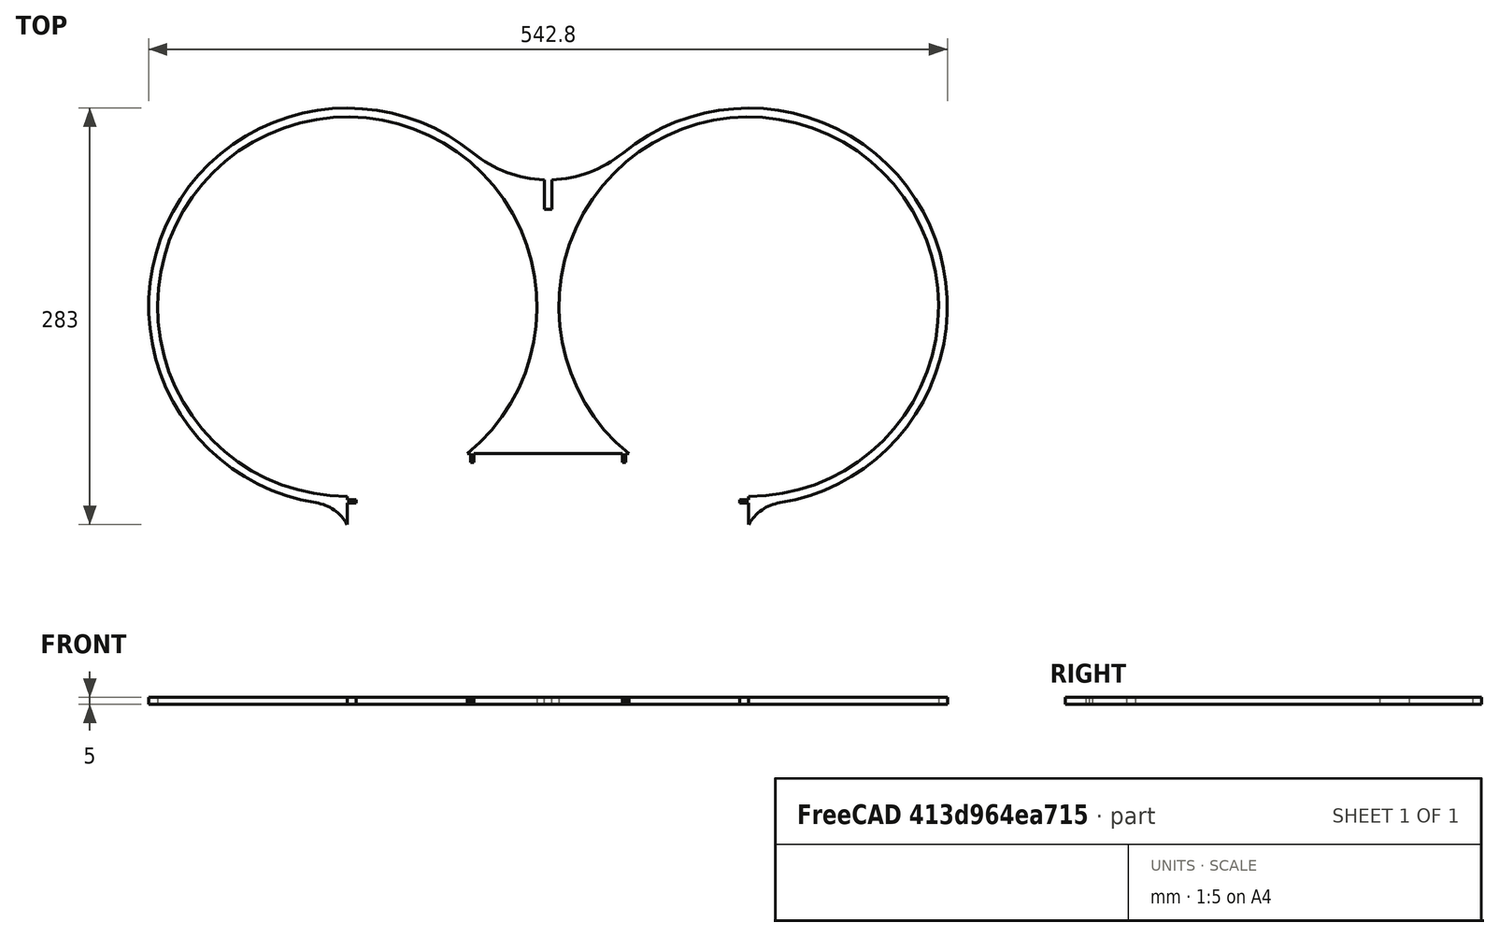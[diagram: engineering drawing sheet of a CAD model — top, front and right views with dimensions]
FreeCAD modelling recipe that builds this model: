
FCSTD DOCUMENT  (FreeCAD 0.16R6706 (Git))
Label: cut_fan
License: All rights reserved
LicenseURL: http://en.wikipedia.org/wiki/All_rights_reserved
objects: Sketcher::SketchObject×3, PartDesign::Pad×1, Part::Part2DObjectPython×1
note: 6 computed .brp shape members not serialized (recipe doc carries the construction recipe); baked Part::Feature solids carry a one-line shape summary decoded from their .brp

FEATURE [Sketcher::SketchObject] Sketch
  sketch-geometry (35):
    g0: ArcOfCircle CenterX=136.4 CenterY=150 CenterZ=0 NormalX=0 NormalY=0 NormalZ=1 Radius=129 StartAngle=4.71231 EndAngle=10.3118
    g1: ArcOfCircle CenterX=-136.4 CenterY=150 CenterZ=0 NormalX=0 NormalY=0 NormalZ=1 Radius=129 StartAngle=5.39616 EndAngle=10.9957
    g2: LineSegment [constr] StartX=-136.39 StartY=2.00014 StartZ=0 EndX=136.39 EndY=2.00014 EndZ=0
    g3: ArcOfCircle CenterX=0 CenterY=316.193 CenterZ=0 NormalX=0 NormalY=0 NormalZ=1 Radius=80 StartAngle=4.02513 EndAngle=4.68113
    g4: ArcOfCircle CenterX=162.407 CenterY=-12.9376 CenterZ=0 NormalX=0 NormalY=0 NormalZ=1 Radius=30 StartAngle=1.72907 EndAngle=2.62039
    g5: ArcOfCircle CenterX=-162.407 CenterY=-12.9376 CenterZ=0 NormalX=0 NormalY=0 NormalZ=1 Radius=30 StartAngle=0.521204 EndAngle=1.41252
    g6: ArcOfCircle CenterX=-136.4 CenterY=150 CenterZ=0 NormalX=0 NormalY=0 NormalZ=1 Radius=135 StartAngle=0.88354 EndAngle=4.55411
    g7: ArcOfCircle CenterX=136.4 CenterY=150 CenterZ=0 NormalX=0 NormalY=0 NormalZ=1 Radius=135 StartAngle=4.87066 EndAngle=8.54124
    g8: LineSegment [constr] StartX=-136.39 StartY=2.00014 StartZ=0 EndX=-136.39 EndY=50 EndZ=0
    g9: LineSegment StartX=-136.39 StartY=21 StartZ=0 EndX=-136.39 EndY=18.7 EndZ=0
    g10: LineSegment StartX=-136.39 StartY=18.7 StartZ=0 EndX=-130.39 EndY=18.7 EndZ=0
    g11: LineSegment StartX=-130.39 StartY=18.7 StartZ=0 EndX=-130.39 EndY=16.5 EndZ=0
    g12: LineSegment StartX=-130.39 StartY=16.5 StartZ=0 EndX=-136.39 EndY=16.5 EndZ=0
    g13: LineSegment [constr] StartX=136.39 StartY=50 StartZ=0 EndX=-136.39 EndY=50 EndZ=0
    g14: LineSegment StartX=-54.9077 StartY=50 StartZ=0 EndX=-52.7077 EndY=50 EndZ=0
    g15: LineSegment StartX=-52.7077 StartY=50 StartZ=0 EndX=-52.7077 EndY=44 EndZ=0
    g16: LineSegment StartX=-52.7077 StartY=44 StartZ=0 EndX=-50.5077 EndY=44 EndZ=0
    g17: LineSegment StartX=-50.5077 StartY=44 StartZ=0 EndX=-50.5077 EndY=50 EndZ=0
    g18: LineSegment StartX=-50.5077 StartY=50 StartZ=0 EndX=50.5077 EndY=50 EndZ=0
    g19: LineSegment StartX=50.5077 StartY=50 StartZ=0 EndX=50.5077 EndY=44 EndZ=0
    g20: LineSegment StartX=50.5077 StartY=44 StartZ=0 EndX=52.7077 EndY=44 EndZ=0
    g21: LineSegment StartX=52.7077 StartY=44 StartZ=0 EndX=52.7077 EndY=50 EndZ=0
    g22: LineSegment StartX=52.7077 StartY=50 StartZ=0 EndX=54.9077 EndY=50 EndZ=0
    g23: LineSegment [constr] StartX=136.39 StartY=50 StartZ=0 EndX=136.39 EndY=2.00014 EndZ=0
    g24: LineSegment StartX=136.39 StartY=21 StartZ=0 EndX=136.39 EndY=18.7 EndZ=0
    g25: LineSegment StartX=136.39 StartY=18.7 StartZ=0 EndX=130.39 EndY=18.7 EndZ=0
    g26: LineSegment StartX=130.39 StartY=18.7 StartZ=0 EndX=130.39 EndY=16.5 EndZ=0
    g27: LineSegment StartX=130.39 StartY=16.5 StartZ=0 EndX=136.39 EndY=16.5 EndZ=0
    g28: LineSegment StartX=136.39 StartY=16.5 StartZ=0 EndX=136.39 EndY=2.00014 EndZ=0
    g29: LineSegment [constr] StartX=-2.5 StartY=236.232 StartZ=0 EndX=2.5 EndY=236.232 EndZ=0
    g30: LineSegment StartX=2.5 StartY=236.232 StartZ=0 EndX=2.5 EndY=216.232 EndZ=0
    g31: LineSegment StartX=2.5 StartY=216.232 StartZ=0 EndX=-2.5 EndY=216.232 EndZ=0
    g32: LineSegment StartX=-2.5 StartY=216.232 StartZ=0 EndX=-2.5 EndY=236.232 EndZ=0
    g33: ArcOfCircle CenterX=0 CenterY=316.193 CenterZ=0 NormalX=0 NormalY=0 NormalZ=1 Radius=80 StartAngle=4.74364 EndAngle=5.39965
    g34: LineSegment StartX=-136.39 StartY=16.5 StartZ=0 EndX=-136.39 EndY=2.00014 EndZ=0
  constraints (105):
    c: Equal(g1,g0)
    c: Symmetric(g0,g1,g-2)
    c: Radius(g0) = 129
    c: DistanceX(g0) = 136.4
    c: DistanceY(g0) = 150
    c: Horizontal(g2)
    c: Symmetric(g2,g2,g-2)
    c: PointOnObject(g3,g-2)
    c: Radius(g3) = 80
    c: Coincident(g4,g2)
    c: Equal(g5,g4)
    c: Radius(g5) = 30
    c: DistanceY(g-1,g13) = 50
    c: Coincident(g6,g1)
    c: Coincident(g6,g5)
    c: Coincident(g6,g3)
    c: Coincident(g7,g0)
    c: Coincident(g7,g4)
    c: Coincident(g7,g33)
    c: Radius(g6) = 135
    c: Radius(g7) = 135
    c: Tangent(g3,g6)
    c: Tangent(g33,g7) = 1.5708
    c: Tangent(g4,g7) = 1.5708
    c: Tangent(g5,g6) = 1.5708
    c: Coincident(g8,g2)
    c: Vertical(g8)
    c: PointOnObject(g1,g8)
    c: Coincident(g9,g1)
    c: PointOnObject(g9,g8)
    c: Coincident(g10,g9)
    c: Horizontal(g10)
    c: Coincident(g11,g10)
    c: Vertical(g11)
    c: PointOnObject(g12,g8)
    c: Horizontal(g12)
    c: Coincident(g11,g12)
    c: Coincident(g13,g8)
    c: Horizontal(g13)
    c: PointOnObject(g1,g13)
    c: PointOnObject(g0,g13)
    c: Coincident(g14,g1)
    c: PointOnObject(g14,g13)
    c: Coincident(g15,g14)
    c: Vertical(g15)
    c: Coincident(g16,g15)
    c: Coincident(g17,g16)
    c: PointOnObject(g17,g13)
    c: Coincident(g18,g17)
    c: PointOnObject(g18,g13)
    c: Coincident(g19,g18)
    c: Vertical(g19)
    c: Coincident(g20,g19)
    c: PointOnObject(g21,g13)
    c: Coincident(g22,g21)
    c: Coincident(g22,g0)
    c: Vertical(g21)
    c: Vertical(g17)
    c: Horizontal(g20)
    c: Horizontal(g16)
    c: Coincident(g20,g21)
    c: Coincident(g23,g13)
    c: Coincident(g23,g2)
    c: Vertical(g23)
    c: PointOnObject(g0,g23)
    c: Coincident(g24,g0)
    c: PointOnObject(g24,g23)
    c: Coincident(g25,g24)
    c: Horizontal(g25)
    c: Coincident(g26,g25)
    c: Vertical(g26)
    c: Coincident(g27,g26)
    c: PointOnObject(g27,g23)
    c: Horizontal(g27)
    c: Coincident(g28,g27)
    c: Coincident(g28,g2)
    c: Equal(g25,g19)
    c: Equal(g19,g17)
    c: Equal(g17,g10)
    c: Equal(g11,g16)
    c: Equal(g16,g20)
    c: Equal(g20,g26)
    c: Symmetric(g19,g16,g-2)
    c: Symmetric(g25,g10,g-2)
    c: Distance(g26) = 2.2
    c: DistanceY(g9,g1) = 2.3
    c: Distance(g12) = 6
    c: DistanceX(g1,g15) = 2.2
    c: Coincident(g30,g31)
    c: Coincident(g31,g32)
    c: Horizontal(g29)
    c: Horizontal(g31)
    c: Vertical(g30)
    c: Vertical(g32)
    c: PointOnObject(g32,g3)
    c: Distance(g31) = 5
    c: Distance(g30) = 20
    c: PointOnObject(g30,g3)
    c: Equal(g3,g33)
    c: Coincident(g3,g29)
    c: Coincident(g33,g29)
    c: Coincident(g3,g33)
    c: Coincident(g2,g5)
    c: Coincident(g34,g12)
    c: Coincident(g34,g2)
FEATURE [PartDesign::Pad] Pad
  Length = 5
  Length2 = 100
  Sketch = -> Sketch
  Type = 0
FEATURE [Part::Part2DObjectPython] Shape2DView  # Draft 2D object (typed FeaturePython)
  Base = -> Pad
  FaceNumbers = [11]
  HiddenLines = false
  Projection = (0,0,1)
  ProjectionMode = 0
  SegmentLength = 0.05
  Tessellation = false
FEATURE [Sketcher::SketchObject] Sketch002
  sketch-geometry (28):
    g0: LineSegment StartX=-392.221 StartY=-72.7258 StartZ=0 EndX=-378.521 EndY=-72.7258 EndZ=0
    g1: LineSegment StartX=-122.221 StartY=-72.7258 StartZ=0 EndX=-122.221 EndY=-329.726 EndZ=0
    g2: LineSegment StartX=-122.221 StartY=-329.726 StartZ=0 EndX=-348.521 EndY=-329.726 EndZ=0
    g3: LineSegment StartX=-392.221 StartY=-329.726 StartZ=0 EndX=-392.221 EndY=-72.7258 EndZ=0
    g4: LineSegment StartX=-348.521 StartY=-72.7258 StartZ=0 EndX=-348.521 EndY=-87.7258 EndZ=0
    g5: LineSegment StartX=-369.521 StartY=-102.726 StartZ=0 EndX=-378.521 EndY=-102.726 EndZ=0
    g6: LineSegment StartX=-378.521 StartY=-102.726 StartZ=0 EndX=-378.521 EndY=-72.7258 EndZ=0
    g7: LineSegment StartX=-348.521 StartY=-329.726 StartZ=0 EndX=-348.521 EndY=-314.726 EndZ=0
    g8: LineSegment StartX=-369.521 StartY=-299.726 StartZ=0 EndX=-378.521 EndY=-299.726 EndZ=0
    g9: LineSegment StartX=-378.521 StartY=-299.726 StartZ=0 EndX=-378.521 EndY=-329.726 EndZ=0
    g10: LineSegment StartX=-132.221 StartY=-198.726 StartZ=0 EndX=-141.221 EndY=-198.726 EndZ=0
    g11: LineSegment StartX=-141.221 StartY=-198.726 StartZ=0 EndX=-141.221 EndY=-203.726 EndZ=0
    g12: LineSegment StartX=-141.221 StartY=-203.726 StartZ=0 EndX=-132.221 EndY=-203.726 EndZ=0
    g13: LineSegment StartX=-132.221 StartY=-203.726 StartZ=0 EndX=-132.221 EndY=-198.726 EndZ=0
    g14: LineSegment StartX=-191.221 StartY=-157.726 StartZ=0 EndX=-311.221 EndY=-157.726 EndZ=0
    g15: LineSegment StartX=-311.221 StartY=-157.726 StartZ=0 EndX=-311.221 EndY=-244.726 EndZ=0
    g16: LineSegment StartX=-311.221 StartY=-244.726 StartZ=0 EndX=-191.221 EndY=-244.726 EndZ=0
    g17: LineSegment StartX=-191.221 StartY=-244.726 StartZ=0 EndX=-191.221 EndY=-157.726 EndZ=0
    g18: LineSegment StartX=-378.521 StartY=-329.726 StartZ=0 EndX=-392.221 EndY=-329.726 EndZ=0
    g19: LineSegment StartX=-348.521 StartY=-72.7258 StartZ=0 EndX=-122.221 EndY=-72.7258 EndZ=0
    g20: LineSegment StartX=-369.521 StartY=-102.726 StartZ=0 EndX=-369.521 EndY=-87.7258 EndZ=0
    g21: LineSegment StartX=-369.521 StartY=-87.7258 StartZ=0 EndX=-348.521 EndY=-87.7258 EndZ=0
    g22: LineSegment StartX=-369.521 StartY=-299.726 StartZ=0 EndX=-369.521 EndY=-314.726 EndZ=0
    g23: LineSegment StartX=-369.521 StartY=-314.726 StartZ=0 EndX=-348.521 EndY=-314.726 EndZ=0
    g24: LineSegment [constr] StartX=-122.221 StartY=-201.226 StartZ=0 EndX=-392.221 EndY=-201.226 EndZ=0
    g25: LineSegment [constr] StartX=-257.221 StartY=-72.7258 StartZ=0 EndX=-257.221 EndY=-329.726 EndZ=0
    g26: GeomPoint [constr] X=-257.221 Y=-201.226 Z=0
    g27: GeomPoint [constr] X=-257.221 Y=-201.226 Z=0
  constraints (83):
    c: Coincident(g19,g1)
    c: Coincident(g1,g2)
    c: Coincident(g18,g3)
    c: Coincident(g3,g0)
    c: Horizontal(g0)
    c: Horizontal(g2)
    c: Vertical(g1)
    c: Vertical(g3)
    c: Coincident(g5,g6)
    c: Horizontal(g5)
    c: Vertical(g4)
    c: Vertical(g6)
    c: PointOnObject(g6,g0)
    c: Coincident(g8,g9)
    c: Horizontal(g8)
    c: Vertical(g7)
    c: Vertical(g9)
    c: PointOnObject(g9,g2)
    c: Coincident(g10,g11)
    c: Coincident(g11,g12)
    c: Coincident(g12,g13)
    c: Coincident(g13,g10)
    c: Horizontal(g10)
    c: Horizontal(g12)
    c: Vertical(g11)
    c: Vertical(g13)
    c: Coincident(g14,g15)
    c: Coincident(g15,g16)
    c: Coincident(g16,g17)
    c: Coincident(g17,g14)
    c: Horizontal(g14)
    c: Horizontal(g16)
    c: Vertical(g15)
    c: Vertical(g17)
    c: PointOnObject(g2,g7)
    c: PointOnObject(g18,g9)
    c: Tangent(g2,g18)
    c: PointOnObject(g0,g6)
    c: PointOnObject(g19,g4)
    c: Tangent(g0,g19)
    c: Equal(g18,g0)
    c: Distance(g18) = 13.7
    c: Equal(g9,g6)
    c: Distance(g6) = 30
    c: Vertical(g20)
    c: Coincident(g20,g21)
    c: Horizontal(g21)
    c: Vertical(g22)
    c: Coincident(g22,g23)
    c: Horizontal(g23)
    c: Coincident(g7,g23)
    c: Coincident(g8,g22)
    c: Coincident(g5,g20)
    c: Coincident(g4,g21)
    c: Coincident(g4,g19)
    c: DistanceX(g0,g4) = 30
    c: Coincident(g2,g7)
    c: Distance(g8) = 9
    c: Distance(g7) = 15
    c: Equal(g7,g4)
    c: Equal(g5,g8)
    c: Equal(g23,g21)
    c: Horizontal(g24)
    c: Symmetric(g1,g1,g24)
    c: Symmetric(g12,g10,g24)
    c: Symmetric(g16,g14,g24)
    c: PointOnObject(g24,g3)
    c: PointOnObject(g25,g19)
    c: PointOnObject(g25,g2)
    c: Vertical(g25)
    c: PointOnObject(g26,g24)
    c: PointOnObject(g27,g25)
    c: Coincident(g27,g26)
    c: Distance(g3) = 257
    c: Distance(g16) = 120
    c: Distance(g15) = 87
    c: DistanceX(g24,g15) = 81
    c: Symmetric(g1,g0,g25)
    c: Distance(g11) = 5
    c: Distance(g10) = 9
    c: DistanceX(g24,g10) = 260
    c: Distance(g24) = 270
    c: PointOnObject(g24,g1)
FEATURE [Sketcher::SketchObject] Sketch001
  sketch-geometry (20):
    g0: LineSegment StartX=-33.6326 StartY=-93.8009 StartZ=0 EndX=-33.6326 EndY=-63.8009 EndZ=0
    g1: LineSegment StartX=-33.6326 StartY=-63.8009 StartZ=0 EndX=98.7016 EndY=-63.8009 EndZ=0
    g2: LineSegment StartX=98.7016 StartY=-63.8009 StartZ=0 EndX=257.867 EndY=-222.967 EndZ=0
    g3: LineSegment StartX=257.867 StartY=-222.967 StartZ=0 EndX=257.867 EndY=-250.001 EndZ=0
    g4: LineSegment StartX=257.867 StartY=-250.001 StartZ=0 EndX=245.367 EndY=-250.001 EndZ=0
    g5: LineSegment StartX=245.367 StartY=-250.001 StartZ=0 EndX=245.367 EndY=-260.001 EndZ=0
    g6: LineSegment StartX=245.367 StartY=-260.001 StartZ=0 EndX=252.367 EndY=-260.001 EndZ=0
    g7: LineSegment StartX=252.367 StartY=-260.001 StartZ=0 EndX=252.367 EndY=-250.001 EndZ=0
    g8: LineSegment StartX=252.367 StartY=-250.001 StartZ=0 EndX=239.867 EndY=-250.001 EndZ=0
    g9: LineSegment StartX=239.867 StartY=-250.001 StartZ=0 EndX=239.867 EndY=-222.967 EndZ=0
    g10: LineSegment StartX=239.867 StartY=-222.967 StartZ=0 EndX=98.7016 EndY=-81.8009 EndZ=0
    g11: LineSegment StartX=98.7016 StartY=-81.8009 StartZ=0 EndX=-28.6326 EndY=-81.8009 EndZ=0
    g12: LineSegment StartX=-28.6326 StartY=-81.8009 StartZ=0 EndX=-28.6326 EndY=-93.8009 EndZ=0
    g13: LineSegment StartX=-24.6326 StartY=-93.8009 StartZ=0 EndX=-24.6326 EndY=-83.8009 EndZ=0
    g14: LineSegment StartX=-24.6326 StartY=-83.8009 StartZ=0 EndX=-29.6326 EndY=-83.8009 EndZ=0
    g15: LineSegment StartX=-29.6326 StartY=-83.8009 StartZ=0 EndX=-29.6326 EndY=-93.8009 EndZ=0
    g16: LineSegment StartX=-29.6326 StartY=-93.8009 StartZ=0 EndX=-33.6326 EndY=-93.8009 EndZ=0
    g17: LineSegment [constr] StartX=257.867 StartY=-222.967 StartZ=0 EndX=239.867 EndY=-222.967 EndZ=0
    g18: LineSegment [constr] StartX=98.7016 StartY=-63.8009 StartZ=0 EndX=98.7016 EndY=-81.8009 EndZ=0
    g19: LineSegment StartX=-28.6326 StartY=-93.8009 StartZ=0 EndX=-24.6326 EndY=-93.8009 EndZ=0
  constraints (55):
    c: Vertical(g0)
    c: Coincident(g0,g1)
    c: Horizontal(g1)
    c: Coincident(g1,g2)
    c: Coincident(g2,g3)
    c: Vertical(g3)
    c: Coincident(g3,g4)
    c: Horizontal(g4)
    c: Coincident(g4,g5)
    c: Vertical(g5)
    c: Coincident(g5,g6)
    c: Horizontal(g6)
    c: Coincident(g6,g7)
    c: Vertical(g7)
    c: Coincident(g7,g8)
    c: Horizontal(g8)
    c: Coincident(g8,g9)
    c: Vertical(g9)
    c: Coincident(g9,g10)
    c: Coincident(g10,g11)
    c: Horizontal(g11)
    c: Coincident(g11,g12)
    c: Vertical(g12)
    c: Vertical(g13)
    c: Coincident(g13,g14)
    c: Horizontal(g14)
    c: Coincident(g14,g15)
    c: Vertical(g15)
    c: Coincident(g15,g16)
    c: Horizontal(g16)
    c: Coincident(g0,g16)
    c: Equal(g15,g13)
    c: Distance(g13) = 10
    c: DistanceY(g8,g0) = 186.2
    c: DistanceY(g10,g1) = 18
    c: DistanceX(g9,g2) = 18
    c: Equal(g5,g7)
    c: Distance(g5) = 10
    c: Distance(g6) = 7
    c: Equal(g8,g4)
    c: Parallel(g2,g10)
    c: Coincident(g17,g2)
    c: Coincident(g17,g9)
    c: Horizontal(g17)
    c: Coincident(g18,g1)
    c: Coincident(g18,g10)
    c: Vertical(g18)
    c: Coincident(g19,g12)
    c: Coincident(g19,g13)
    c: Horizontal(g19)
    c: Equal(g19,g16)
    c: Distance(g14) = 5
    c: Distance(g19) = 4
    c: Distance(g0,g0) = 30
    c: DistanceX(g13,g5) = 270
